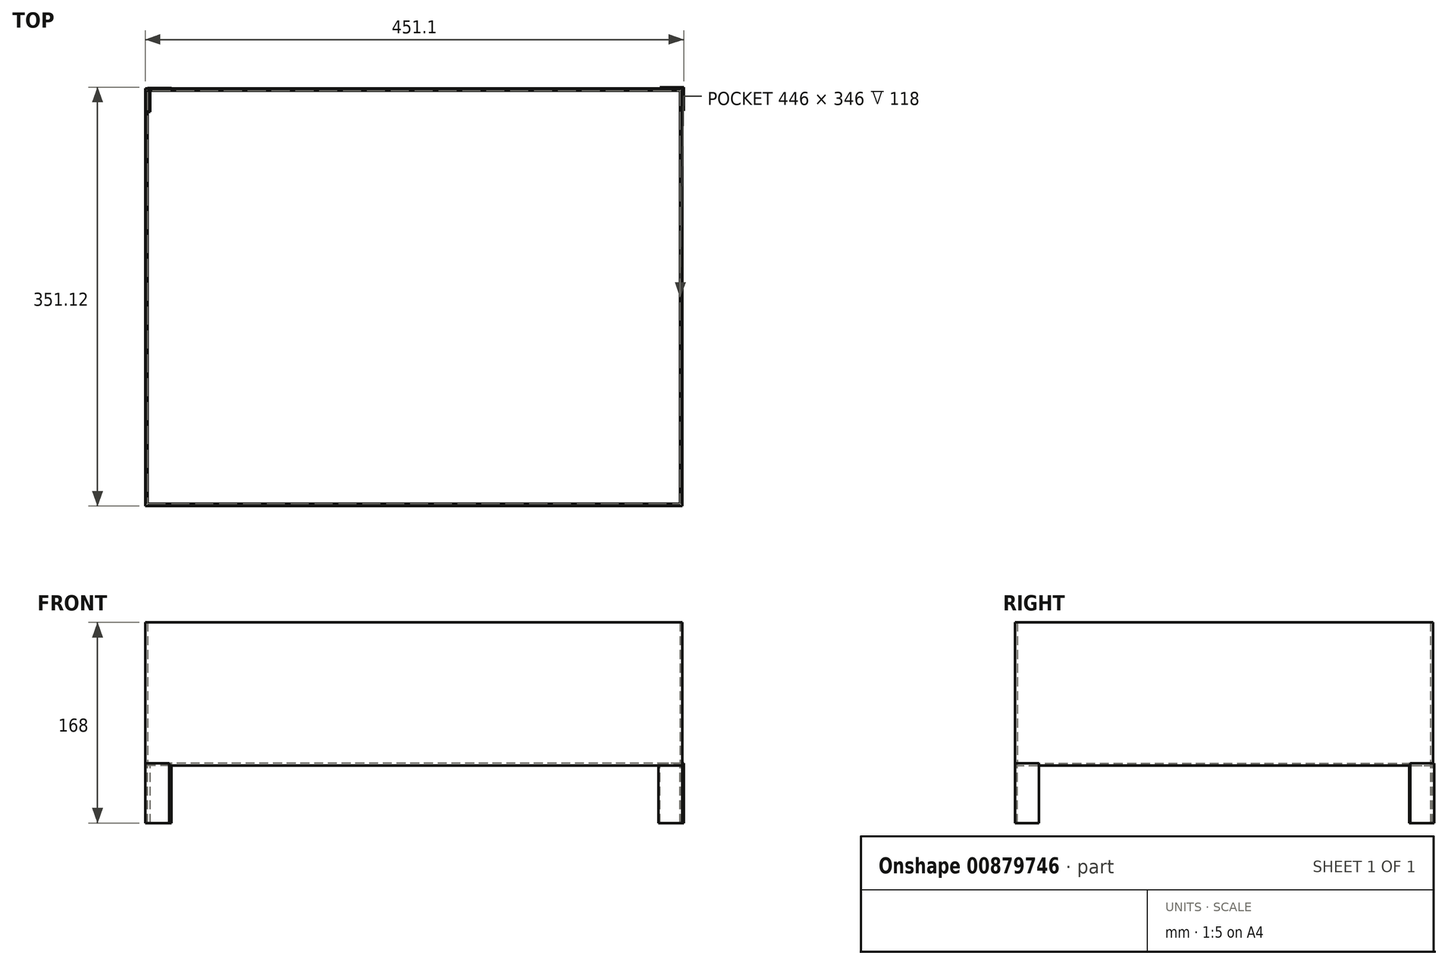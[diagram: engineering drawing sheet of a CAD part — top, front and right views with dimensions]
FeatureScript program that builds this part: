
annotation { "Feature Type Name" : "Feature", "Feature Type Description" : "" }
export const myFeature = defineFeature(function(context is Context, id is Id, definition is map)
    precondition{}
    {
        {
            var Q0;
            Q0=qCreatedBy(makeId("Top.planeOp"),FACE);
            var sketch = newSketch(context, id + "F0", { "sketchPlane" : qUnion([Q0])});
            skLineSegment(sketch, "E0.bottom", {"start": v(225, -175) * mm, "end": v(-225, -175) * mm});
            skLineSegment(sketch, "E0.top", {"start": v(225, 175) * mm, "end": v(-225, 175) * mm});
            skLineSegment(sketch, "E0.left", {"start": v(225, -175) * mm, "end": v(225, 175) * mm});
            skLineSegment(sketch, "E0.right", {"start": v(-225, -175) * mm, "end": v(-225, 175) * mm});
            skPoint(sketch, "E0.middle", {"position": v(0, 0) * mm});
            skLineSegment(sketch, "E1.MirrorCS", {"start": v(-225, 175) * mm, "end": v(-225, -175) * mm});
            skLineSegment(sketch, "E2.MirrorCS", {"start": v(225, 175) * mm, "end": v(225, -175) * mm});
            skLineSegment(sketch, "E3.0", {"start": v(223, 173) * mm, "end": v(-223, 173) * mm});
            skLineSegment(sketch, "E3.1", {"start": v(223, -173) * mm, "end": v(223, 173) * mm});
            skLineSegment(sketch, "E3.2", {"start": v(223, -173) * mm, "end": v(-223, -173) * mm});
            skLineSegment(sketch, "E3.3", {"start": v(-223, 173) * mm, "end": v(-223, -173) * mm});
            skSolve(sketch);
        }
        {
            var Q0;
            Q0 = qSketchRegion(id + "F0", true);
            extrude(context, id + "F1", {"entities" : qUnion([Q0]), "depth" : 120 * mm, "offsetDistance" : 25 * mm});
        }
        {
            var Q0;
            Q0=makeQuery(id+"F0.imprint","IMPRINT",FACE,{"disambiguationData":[TD([[makeQuery(id+"F0.imprint","IMPRINT",EDGE,{"derivedFrom":sQuery(id+"F0.wireOp",EDGE,"E3.0")}),1.0]])]});
            extrude(context, id + "F2", {"entities" : qUnion([Q0]), "operationType" : NewBodyOperationType.ADD, "depth" : 2 * mm, "offsetDistance" : 25 * mm});
        }
        {
            var Q0;
            Q0=makeQuery(id+"F2.opExtrude","CAP_FACE",FACE,{"disambiguationData":[OSD([sQuery(id+"F0.wireOp",EDGE,"E3.0"),sQuery(id+"F0.wireOp",EDGE,"E3.1"),sQuery(id+"F0.wireOp",EDGE,"E3.2"),sQuery(id+"F0.wireOp",EDGE,"E3.3")])],"isStart":false});
            var sketch = newSketch(context, id + "F3", { "sketchPlane" : qUnion([Q0])});
            skLineSegment(sketch, "E4", {"start": v(223, -154.92) * mm, "end": v(225.02, -154.92) * mm});
            skLineSegment(sketch, "E5", {"start": v(225.02, -154.92) * mm, "end": v(225.02, -174.92) * mm});
            skLineSegment(sketch, "E6", {"start": v(225.02, -174.92) * mm, "end": v(205.02, -174.92) * mm});
            skLineSegment(sketch, "E7", {"start": v(205.02, -174.92) * mm, "end": v(205.02, -173) * mm});
            skLineSegment(sketch, "E8", {"start": v(205.02, -173) * mm, "end": v(223, -173) * mm});
            skLineSegment(sketch, "E9", {"start": v(223, -173) * mm, "end": v(223, -154.92) * mm});
            skLineSegment(sketch, "E10", {"start": v(-204.9, -173) * mm, "end": v(-204.9, -175.02) * mm});
            skLineSegment(sketch, "E11", {"start": v(-204.9, -175.02) * mm, "end": v(-224.9, -175.02) * mm});
            skLineSegment(sketch, "E12", {"start": v(-224.9, -175.02) * mm, "end": v(-224.9, -155.02) * mm});
            skLineSegment(sketch, "E13", {"start": v(-224.9, -155.02) * mm, "end": v(-222.98, -155.02) * mm});
            skLineSegment(sketch, "E14", {"start": v(-222.98, -155.02) * mm, "end": v(-222.98, -173) * mm});
            skLineSegment(sketch, "E15", {"start": v(-222.98, -173) * mm, "end": v(-204.9, -173) * mm});
            skLineSegment(sketch, "E16", {"start": v(206.1, 174.08) * mm, "end": v(206.1, 176.1) * mm});
            skLineSegment(sketch, "E17", {"start": v(206.1, 176.1) * mm, "end": v(226.1, 176.1) * mm});
            skLineSegment(sketch, "E18", {"start": v(226.1, 176.1) * mm, "end": v(226.1, 156.1) * mm});
            skLineSegment(sketch, "E19", {"start": v(226.1, 156.1) * mm, "end": v(224.18, 156.1) * mm});
            skLineSegment(sketch, "E20", {"start": v(224.18, 156.1) * mm, "end": v(224.18, 174.08) * mm});
            skLineSegment(sketch, "E21", {"start": v(224.18, 174.08) * mm, "end": v(206.1, 174.08) * mm});
            skLineSegment(sketch, "E22", {"start": v(-220.98, 155.2) * mm, "end": v(-223, 155.2) * mm});
            skLineSegment(sketch, "E23", {"start": v(-223, 155.2) * mm, "end": v(-223, 175.2) * mm});
            skLineSegment(sketch, "E24", {"start": v(-223, 175.2) * mm, "end": v(-203, 175.2) * mm});
            skLineSegment(sketch, "E25", {"start": v(-203, 175.2) * mm, "end": v(-203, 173.28) * mm});
            skLineSegment(sketch, "E26", {"start": v(-203, 173.28) * mm, "end": v(-220.98, 173.28) * mm});
            skLineSegment(sketch, "E27", {"start": v(-220.98, 173.28) * mm, "end": v(-220.98, 155.2) * mm});
            skSolve(sketch);
        }
        {
            var Q0;
            Q0 = qSketchRegion(id + "F3", true);
            var Q1;
            Q1 = qConstructionFilter(qBodyType(qCreatedBy(id + "F3" ,EDGE), BodyType.WIRE), ConstructionObject.NO);
            extrude(context, id + "F4", {"entities" : qUnion([Q0]), "surfaceEntities" : qUnion([Q1]), "oppositeDirection" : true, "depth" : 50 * mm, "offsetDistance" : 25 * mm});
        }
    });
